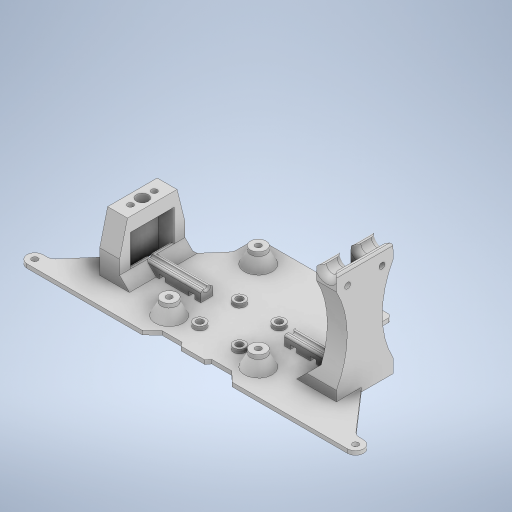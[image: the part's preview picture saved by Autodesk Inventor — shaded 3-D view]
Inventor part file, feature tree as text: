
AUTODESK INVENTOR PART (.ipt)
format: ipt  version: 2023 (Build 270158000, 158)  size: 785,920 bytes
history: native  units: in
note: dims shown in document units (in); Inventor stores cm internally (conversion verified against a paired STEP export)
features: sketch x23, extrude x22, chamfer x5, fillet x4, other x1
ambient origin geometry x8: Origin, YZ Plane, XZ Plane, XY Plane, X Axis, Y Axis, Z Axis, Center Point
bodies: Solid1 (feature_tree)
feature tree (55):
  extrude  "Extrusion1"  Depth=0.315in
  extrude  "Extrusion2"  Depth=0.315in
  extrude  "Extrusion3"  Depth=0.315in
  extrude  "Extrusion4"  Depth=0.0787in TaperAngle=0.0deg
  extrude  "Extrusion5"  Depth=0.315in
  extrude  "Extrusion6"  Depth=0.315in
  extrude  "Extrusion15"  Depth=0.315in
  sketch  "Sketch16"  dims[d27=1.7717in]
  chamfer  "Chamfer2"  Distance=0.315in
  extrude  "Extrusion17"  Depth=0.1575in
  extrude  "Extrusion18"  Depth=0.2362in
  extrude  "Extrusion24"  Depth=0.2362in
  sketch  "Sketch27"  dims[d30=1.7717in]
  extrude  "Extrusion29"  Depth=0.0787in TaperAngle=0.0deg
  extrude  "Extrusion30"  Depth=1.1811in
  extrude  "Extrusion31"  Depth=0.7874in
  extrude  "Extrusion32"  Depth=0.0787in TaperAngle=0.0deg
  fillet  "Fillet3"  Radius=0.0787in
  extrude  "Extrusion33"  Depth=0.0787in TaperAngle=0.0deg
  fillet  "Fillet4"  Radius=0.9843in
  chamfer  "Chamfer5"  Distance=0.1378in
  extrude  "Extrusion34"  Depth=0.0787in
  fillet  "Fillet5"  Radius=0.1181in
  extrude  "Extrusion35"  Depth=0.0787in
  extrude  "Extrusion36"  Depth=0.0787in
  extrude  "Extrusion37"  Depth=0.2362in
  extrude  "Extrusion38"  Depth=0.2362in
  extrude  "Extrusion39"  Depth=0.0787in
  extrude  "Extrusion40"  Depth=0.0787in
  fillet  "Fillet6"  Radius=0.1181in
  chamfer  "Chamfer6"  Distance=0.1969in
  chamfer  "Chamfer7"  Distance=0.1969in
  chamfer  "Chamfer8"  Distance=0.0787in
  sketch  "Sketch1"  dims[d0=0.0984in d1=0.0984in d2=0.1181in d3=0.1181in d4=0.315in]
  sketch  "Sketch2"  dims[d5=0.315in d6=0.315in]
  sketch  "Sketch3"  dims[d7=0.315in d8=2.3622in]
  sketch  "Sketch4"  dims[d18=0.1575in d19=0.0787in d20=0.0in]
  sketch  "Sketch5"  dims[d21=2.3622in d22=0.315in]
  sketch  "Sketch6"  dims[d23=0.315in d24=0.315in]
  sketch  "Sketch15"  dims[d25=0.315in d26=1.7717in]
  sketch  "Sketch17"  dims[d28=1.7717in]
  sketch  "Sketch22"  dims[d29=0.2756in]
  other  "Image1"
  sketch  "Sketch28"  dims[d31=0.2953in d36=0.315in d37=0.0in]
  sketch  "Sketch29"  dims[d38=0.1575in d39=0.0in d40=0.7874in]
  sketch  "Sketch30"  dims[d41=0.7874in d42=0.2362in]
  sketch  "Sketch31"  dims[d43=0.2362in d44=0.2362in]
  sketch  "Sketch32"  dims[d45=0.2362in d46=0.0787in d47=0.0in]
  sketch  "Sketch33"  dims[d49=0.9843in d50=1.1811in]
  sketch  "Sketch34"  dims[d51=2.3622in d52=0.7874in]
  sketch  "Sketch35"  dims[d53=0.9843in d54=0.0787in d55=0.0in d56=0.0787in d57=0.0in]
  sketch  "Sketch36"  dims[d61=0.0787in d62=0.0in d63=0.0787in d64=0.0in d65=0.9843in]
  sketch  "Sketch37"  dims[d66=1.1811in]
  sketch  "Sketch38"  dims[d108=0.1378in]
  sketch  "Sketch39"  dims[d109=0.1378in d110=0.1378in d111=0.1378in d112=0.1181in d113=0.0in d114=0.2402in d115=0.1378in d116=0.2362in d117=0.2362in d118=1.6614in d119=0.2402in d122=0.1181in d123=0.2362in d124=45.0deg d125=0.1969in d126=0.1969in d127=0.0787in d128=0.0in d129=0.0787in d130=0.0in d168=0.1181in d169=0.1181in d170=0.1181in d171=0.1181in d172=0.1969in d173=0.0in d204=1.1024in d205=1.1024in d206=0.1575in d207=0.1575in d209=1.1024in d216=0.3937in d217=2.6575in d218=0.3937in d219=2.6575in d220=0.1575in d221=0.1693in d222=0.1181in d223=1.3189in d224=0.2362in d225=1.1024in d226=0.0315in d227=0.1181in d228=1.3189in d229=0.2362in d230=0.2362in d231=0.2362in d232=0.1969in d233=0.0in d234=0.3937in d235=1.126in d236=2.1654in d237=0.0in d238=0.2362in d239=0.0in d240=0.0in d241=0.2362in d242=1.9685in d243=0.2953in d244=0.0in d245=0.1181in d246=0.4724in d247=0.6811in d248=0.1181in d249=0.1181in d250=0.1969in d251=0.2953in d252=0.0in d253=0.0394in d254=1.7717in d255=1.7717in d256=0.3937in d257=0.0787in d258=45.0deg d259=0.0787in d260=0.3937in d261=0.0in d262=0.0394in d263=0.1181in d264=0.3937in d265=0.1181in d266=0.0787in d267=0.1181in d268=0.0787in d269=0.3937in d270=0.0in d272=0.5315in d273=0.5315in d274=1.1024in d275=0.0in d276=0.2362in d277=1.1024in d278=0.0in d279=0.315in d280=0.8661in d281=0.6299in d282=0.315in d283=0.0in d285=0.3937in d286=0.0in d287=0.2362in d288=0.8661in d289=0.1181in d290=0.5906in d291=0.1181in d292=0.0787in d293=0.1181in d294=0.0787in d295=0.0in d296=0.0787in d297=0.3937in d298=0.0in d299=0.0394in d300=0.1575in d301=0.6299in d302=45.0deg d303=0.1575in d304=0.6299in d305=45.0deg d306=0.2362in d307=0.2362in d308=0.1181in d309=0.1181in d310=0.1969in d311=0.6299in d312=45.0deg d313=0.315in d314=0.0787in d142=0.0in d143=0.0in d144=0.0in d145=0.0in d182=0.0197in d183=0.0344in d184=0.0197in d185=0.0344in d215=0.0197in]
